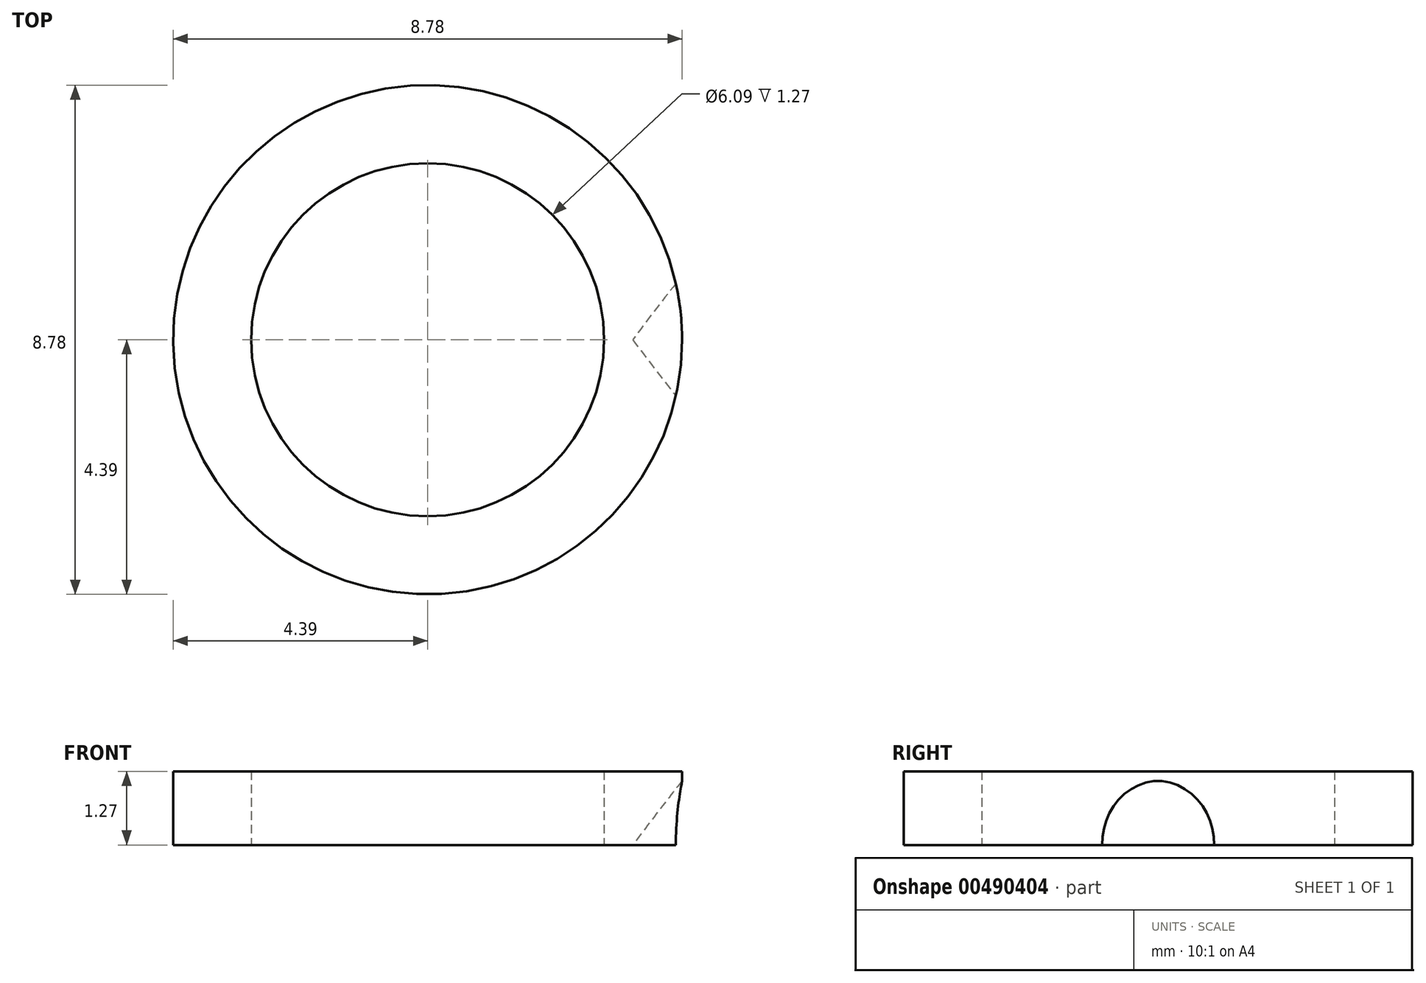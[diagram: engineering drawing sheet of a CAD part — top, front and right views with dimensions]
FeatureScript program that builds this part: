
annotation { "Feature Type Name" : "Feature", "Feature Type Description" : "" }
export const myFeature = defineFeature(function(context is Context, id is Id, definition is map)
    precondition{}
    {
        {
            var Q0;
            Q0=qCreatedBy(makeId("Front.planeOp"),FACE);
            var sketch = newSketch(context, id + "F0", { "sketchPlane" : qUnion([Q0])});
            skArc(sketch, "E0", {"start": v(37.28, 0) * mm, "mid": v(3.27, 17.08) * mm, "end": v(-30.75, 0) * mm});
            skLineSegment(sketch, "E1", {"start": v(-30.75, 0) * mm, "end": v(37.28, 0) * mm});
            skSolve(sketch);
        }
        {
            var Q0;
            Q0=makeQuery(id+"F0.imprint","IMPRINT",FACE,{"disambiguationData":[TD([[makeQuery(id+"F0.imprint","IMPRINT",EDGE,{"derivedFrom":sQuery(id+"F0.wireOp",EDGE,"E0")}),1.0]])]});
            var Q1;
            Q1=sQuery(id+"F0.wireOp",EDGE,"E1");
            revolve(context, id + "F1", {"entities" : qUnion([Q0]), "axis" : qUnion([Q1]), "revolveType" : RevolveType.FULL});
        }
        {
            var Q0;
            Q0=qCreatedBy(makeId("Top.planeOp"),FACE);
            var sketch = newSketch(context, id + "F2", { "sketchPlane" : qUnion([Q0])});
            skCircle(sketch, "E2", {"center": v(-34.3, 0) * mm, "radius": 4.39 * mm});
            skCircle(sketch, "E3", {"center": v(-34.3, 0) * mm, "radius": 3.04 * mm});
            skSolve(sketch);
        }
        {
            var Q0;
            Q0 = qSketchRegion(id + "F2", true);
            extrude(context, id + "F3", {"entities" : qUnion([Q0]), "operationType" : NewBodyOperationType.ADD, "depth" : 1.27 * mm});
        }
    });
